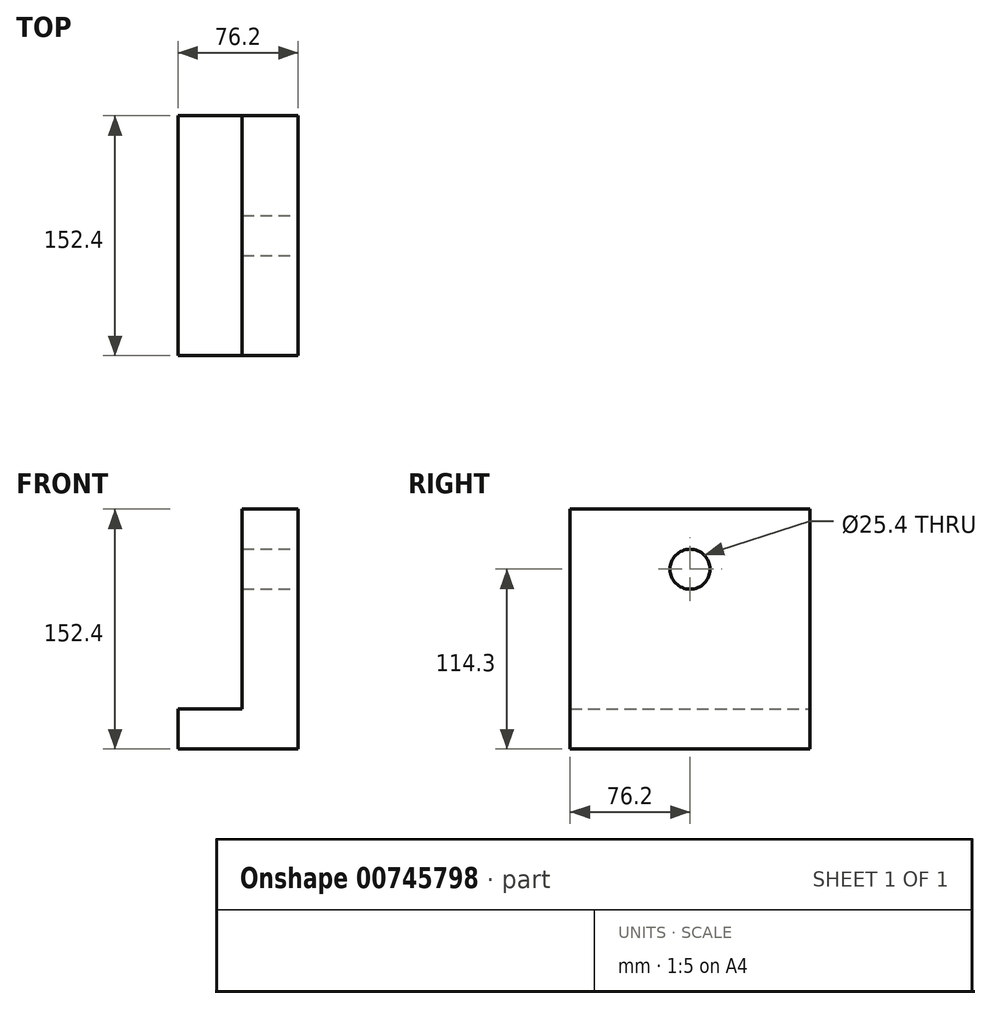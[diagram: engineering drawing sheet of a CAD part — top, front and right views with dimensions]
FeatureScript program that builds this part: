
annotation { "Feature Type Name" : "Feature", "Feature Type Description" : "" }
export const myFeature = defineFeature(function(context is Context, id is Id, definition is map)
    precondition{}
    {
        {
            var Q0;
            Q0=qCreatedBy(makeId("Front.planeOp"),FACE);
            var sketch = newSketch(context, id + "F0", { "sketchPlane" : qUnion([Q0])});
            skLineSegment(sketch, "E0", {"start": v(0, 152.4) * mm, "end": v(0, 0) * mm});
            skLineSegment(sketch, "E1", {"start": v(0, 0) * mm, "end": v(-76.2, 0) * mm});
            skLineSegment(sketch, "E2", {"start": v(-76.2, 0) * mm, "end": v(-76.2, 25.4) * mm});
            skLineSegment(sketch, "E3", {"start": v(-76.2, 25.4) * mm, "end": v(-35.46, 25.4) * mm});
            skLineSegment(sketch, "E4", {"start": v(-35.46, 25.4) * mm, "end": v(-35.46, 152.4) * mm});
            skLineSegment(sketch, "E5", {"start": v(-35.46, 152.4) * mm, "end": v(0, 152.4) * mm});
            skSolve(sketch);
        }
        {
            var Q0;
            Q0 = qSketchRegion(id + "F0", true);
            var Q1;
            Q1=makeQuery(id+"F0.imprint","IMPRINT",FACE,{"disambiguationData":[TD([[makeQuery(id+"F0.imprint","IMPRINT",EDGE,{"derivedFrom":sQuery(id+"F0.wireOp",EDGE,"E0")}),-1.0]])]});
            extrude(context, id + "F1", {"entities" : qUnion([Q0, Q1]), "endBound" : BoundingType.SYMMETRIC, "depth" : 152.4 * mm, "offsetDistance" : 25.4 * mm});
        }
        {
            var Q0;
            Q0=makeQuery(id+"F1.opExtrude","SWEPT_FACE",FACE,{"disambiguationData":[OSD([sQuery(id+"F0.wireOp",EDGE,"E0")])]});
            var sketch = newSketch(context, id + "F2", { "sketchPlane" : qUnion([Q0])});
            skCircle(sketch, "E6", {"center": v(0, 114.3) * mm, "radius": 12.7 * mm});
            skSolve(sketch);
        }
        {
            var Q0;
            Q0=makeQuery(id+"F2.imprint","IMPRINT",FACE,{"disambiguationData":[TD([[makeQuery(id+"F2.imprint","IMPRINT",EDGE,{"derivedFrom":sQuery(id+"F2.wireOp",EDGE,"E6")}),1.0]])]});
            extrude(context, id + "F3", {"entities" : qUnion([Q0]), "operationType" : NewBodyOperationType.REMOVE, "endBound" : BoundingType.THROUGH_ALL, "oppositeDirection" : true, "depth" : 25.4 * mm, "offsetDistance" : 25.4 * mm});
        }
    });
